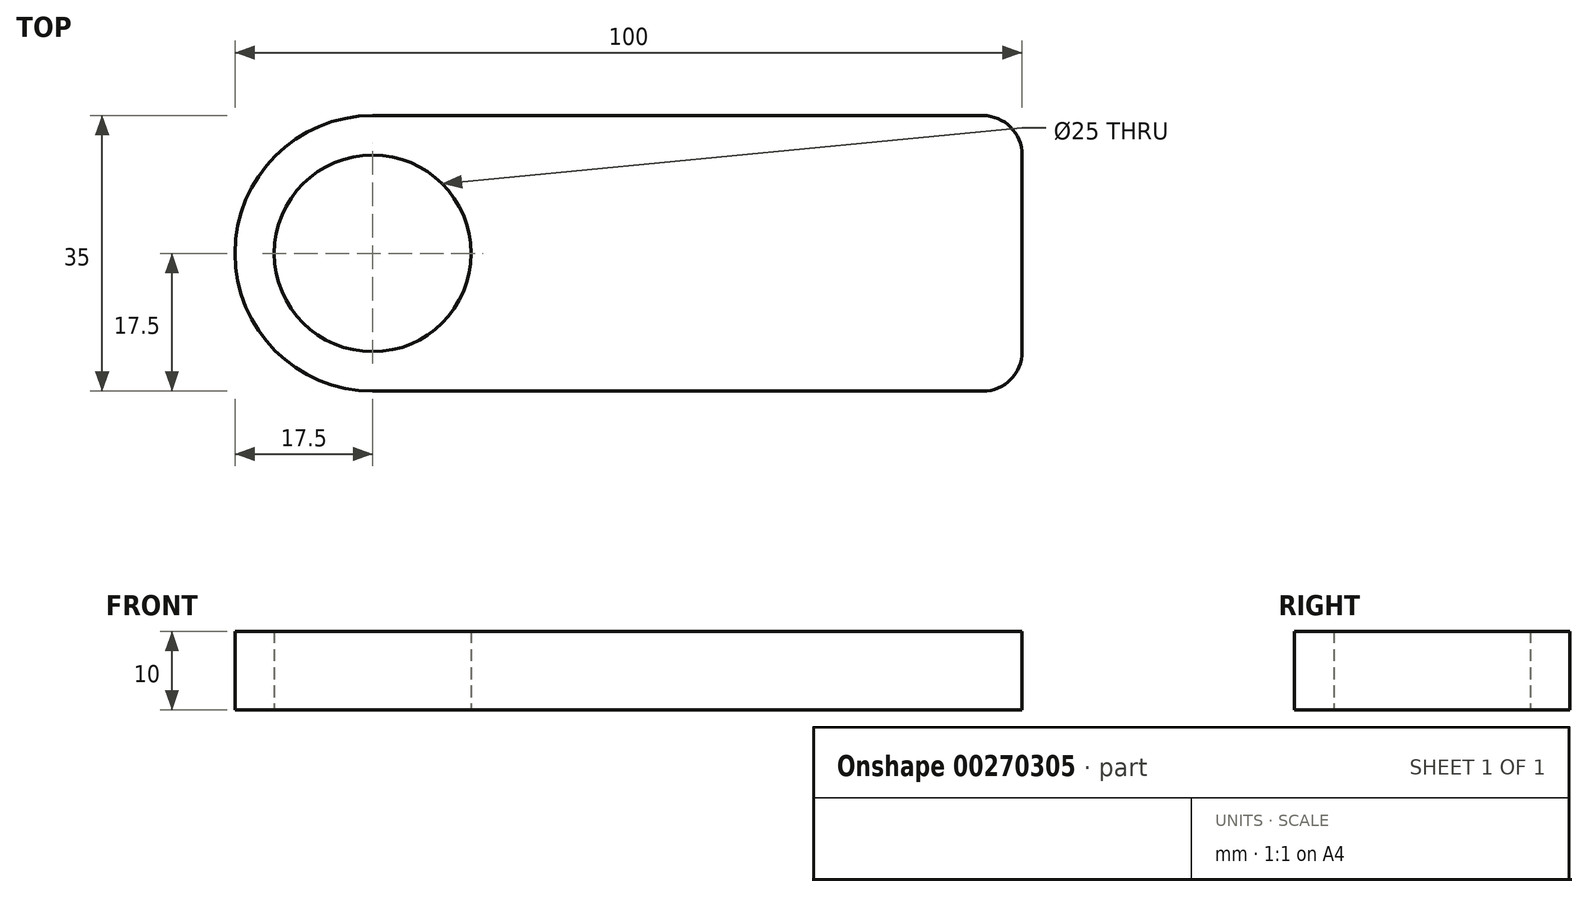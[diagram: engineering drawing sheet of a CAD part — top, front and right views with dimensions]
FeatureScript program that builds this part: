
annotation { "Feature Type Name" : "Feature", "Feature Type Description" : "" }
export const myFeature = defineFeature(function(context is Context, id is Id, definition is map)
    precondition{}
    {
        {
            var Q0;
            Q0=qCreatedBy(makeId("Top.planeOp"),FACE);
            var sketch = newSketch(context, id + "F0", { "sketchPlane" : qUnion([Q0])});
            skLineSegment(sketch, "E0.bottom", {"start": v(17.5, 0) * mm, "end": v(95, 0) * mm});
            skLineSegment(sketch, "E0.top", {"start": v(17.5, 35) * mm, "end": v(95, 35) * mm});
            skLineSegment(sketch, "E0.left", {"start": v(0, 17.5) * mm, "end": v(0, 17.5) * mm});
            skLineSegment(sketch, "E0.right", {"start": v(100, 5) * mm, "end": v(100, 30) * mm});
            skLineSegment(sketch, "E1.bottom", {"start": v(0, 0) * mm, "end": v(17.5, 0) * mm, "construction": true});
            skLineSegment(sketch, "E1.top", {"start": v(0, 17.5) * mm, "end": v(17.5, 17.5) * mm, "construction": true});
            skLineSegment(sketch, "E1.left", {"start": v(0, 0) * mm, "end": v(0, 17.5) * mm, "construction": true});
            skLineSegment(sketch, "E1.right", {"start": v(17.5, 0) * mm, "end": v(17.5, 17.5) * mm, "construction": true});
            skCircle(sketch, "E2", {"center": v(17.5, 17.5) * mm, "radius": 12.5 * mm});
            skPoint(sketch, "E3.visualSharp", {"position": v(0, 0) * mm});
            skArc(sketch, "E3.filletArc", {"start": v(0, 17.5) * mm, "mid": v(5.13, 5.13) * mm, "end": v(17.5, 0) * mm});
            skPoint(sketch, "E4.visualSharp", {"position": v(0, 35) * mm});
            skArc(sketch, "E4.filletArc", {"start": v(17.5, 35) * mm, "mid": v(5.13, 29.87) * mm, "end": v(0, 17.5) * mm});
            skPoint(sketch, "E5.visualSharp", {"position": v(100, 35) * mm});
            skArc(sketch, "E5.filletArc", {"start": v(100, 30) * mm, "mid": v(98.54, 33.54) * mm, "end": v(95, 35) * mm});
            skPoint(sketch, "E6.visualSharp", {"position": v(100, 0) * mm});
            skArc(sketch, "E6.filletArc", {"start": v(95, 0) * mm, "mid": v(98.54, 1.46) * mm, "end": v(100, 5) * mm});
            skSolve(sketch);
        }
        {
            var Q0;
            Q0=makeQuery(id+"F0.imprint","IMPRINT",FACE,{"disambiguationData":[TD([[makeQuery(id+"F0.imprint","IMPRINT",EDGE,{"derivedFrom":sQuery(id+"F0.wireOp",EDGE,"E0.bottom")}),1.0]])]});
            extrude(context, id + "F1", {"entities" : qUnion([Q0]), "depth" : 10 * mm});
        }
    });
